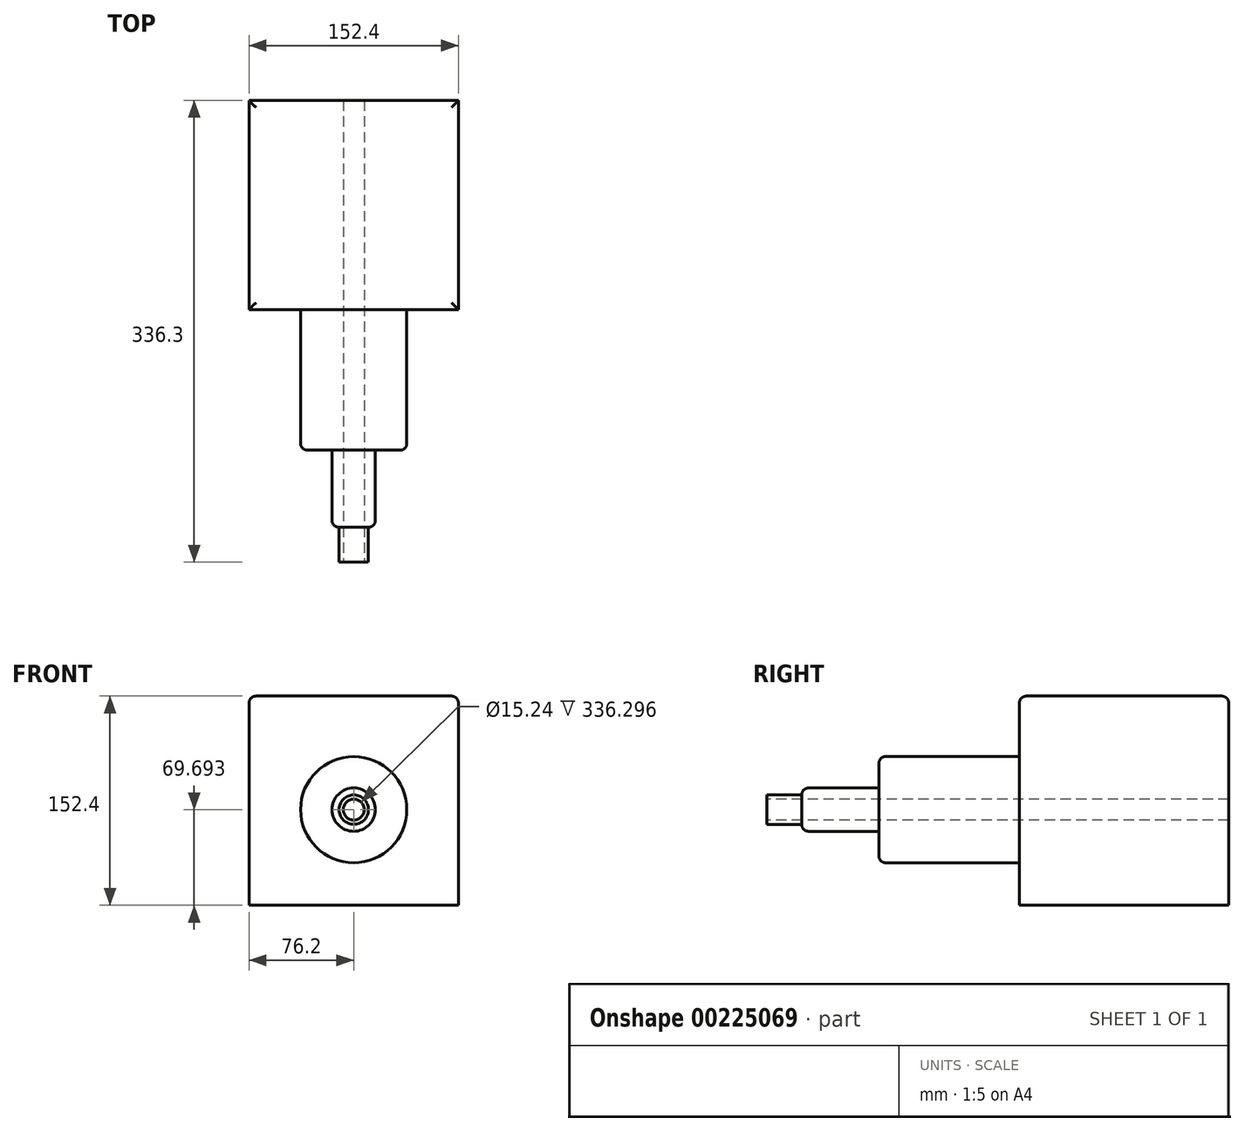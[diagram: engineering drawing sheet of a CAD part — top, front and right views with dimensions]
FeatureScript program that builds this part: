
annotation { "Feature Type Name" : "Feature", "Feature Type Description" : "" }
export const myFeature = defineFeature(function(context is Context, id is Id, definition is map)
    precondition{}
    {
        {
            var Q0;
            Q0=qCreatedBy(makeId("Top.planeOp"),FACE);
            var sketch = newSketch(context, id + "F0", { "sketchPlane" : qUnion([Q0])});
            skLineSegment(sketch, "E0.bottom", {"start": v(76.2, 76.2) * mm, "end": v(-76.2, 76.2) * mm});
            skLineSegment(sketch, "E0.top", {"start": v(76.2, -76.2) * mm, "end": v(-76.2, -76.2) * mm});
            skLineSegment(sketch, "E0.left", {"start": v(76.2, 76.2) * mm, "end": v(76.2, -76.2) * mm});
            skLineSegment(sketch, "E0.right", {"start": v(-76.2, 76.2) * mm, "end": v(-76.2, -76.2) * mm});
            skPoint(sketch, "E0.middle", {"position": v(0, 0) * mm});
            skSolve(sketch);
        }
        {
            var Q0;
            Q0 = qSketchRegion(id + "F0", true);
            extrude(context, id + "F1", {"entities" : qUnion([Q0]), "depth" : 152.4 * mm});
        }
        {
            var Q0;
            Q0=makeQuery(id+"F1.opExtrude","CAP_FACE",FACE,{"disambiguationData":[OSD([sQuery(id+"F0.wireOp",EDGE,"E0.bottom"),sQuery(id+"F0.wireOp",EDGE,"E0.top"),sQuery(id+"F0.wireOp",EDGE,"E0.left"),sQuery(id+"F0.wireOp",EDGE,"E0.right")])],"isStart":false});
            fillet(context, id + "F2", {"entities" : qUnion([Q0]), "radius" : 5.08 * mm, "tangentPropagation" : true, "allowEdgeOverflow" : false});
        }
        {
            var Q0;
            Q0=makeQuery(id+"F1.opExtrude","SWEPT_FACE",FACE,{"disambiguationData":[OSD([sQuery(id+"F0.wireOp",EDGE,"E0.top")])]});
            var sketch = newSketch(context, id + "F3", { "sketchPlane" : qUnion([Q0])});
            skCircle(sketch, "E1", {"center": v(0, 69.7) * mm, "radius": 38.66 * mm});
            skSolve(sketch);
        }
        {
            var Q0;
            Q0 = qSketchRegion(id + "F3", true);
            extrude(context, id + "F4", {"entities" : qUnion([Q0]), "operationType" : NewBodyOperationType.ADD, "depth" : 102.36 * mm});
        }
        {
            var Q0;
            Q0=makeQuery(id+"F4.opExtrude","CAP_FACE",FACE,{"disambiguationData":[OSD([sQuery(id+"F3.wireOp",EDGE,"E1")])],"isStart":false});
            var sketch = newSketch(context, id + "F5", { "sketchPlane" : qUnion([Q0])});
            skCircle(sketch, "E2", {"center": v(0, 69.7) * mm, "radius": 15.78 * mm});
            skSolve(sketch);
        }
        {
            var Q0;
            Q0 = qSketchRegion(id + "F5", true);
            extrude(context, id + "F6", {"entities" : qUnion([Q0]), "operationType" : NewBodyOperationType.ADD, "depth" : 56.13 * mm});
        }
        {
            var Q0;
            Q0=makeQuery(id+"F6.opExtrude","CAP_EDGE",EDGE,{"disambiguationData":[OSD([sQuery(id+"F5.wireOp",EDGE,"E2")])],"isStart":false});
            var Q1;
            Q1=makeQuery(id+"F6.opExtrude","CAP_EDGE",EDGE,{"disambiguationData":[OSD([sQuery(id+"F5.wireOp",EDGE,"E2")])],"isStart":true});
            var Q2;
            Q2=makeQuery(id+"F4.opExtrude","CAP_EDGE",EDGE,{"disambiguationData":[OSD([sQuery(id+"F3.wireOp",EDGE,"E1")])],"isStart":false});
            var Q3;
            Q3=makeQuery(id+"F4.opExtrude","CAP_EDGE",EDGE,{"disambiguationData":[OSD([sQuery(id+"F3.wireOp",EDGE,"E1")])],"isStart":true});
            fillet(context, id + "F7", {"entities" : qUnion([Q0, Q1, Q2, Q3]), "radius" : 5.08 * mm, "tangentPropagation" : true, "allowEdgeOverflow" : false});
        }
        {
            var Q0;
            Q0=makeQuery(id+"F6.opExtrude","CAP_FACE",FACE,{"disambiguationData":[OSD([sQuery(id+"F5.wireOp",EDGE,"E2")])],"isStart":false});
            var sketch = newSketch(context, id + "F8", { "sketchPlane" : qUnion([Q0])});
            skCircle(sketch, "E3", {"center": v(0, 69.7) * mm, "radius": 5.43 * mm});
            skSolve(sketch);
        }
        {
            var Q0;
            Q0=sQuery(id+"F8.wireOp",VERTEX,"E3.center");
            var Q1;
            Q1=makeQuery(id+"F1.opExtrude","SWEPT_BODY",BODY,{"disambiguationData":[OSD([sQuery(id+"F0.wireOp",EDGE,"E0.bottom"),sQuery(id+"F0.wireOp",EDGE,"E0.top"),sQuery(id+"F0.wireOp",EDGE,"E0.left"),sQuery(id+"F0.wireOp",EDGE,"E0.right")])]});
            hole(context, id + "F9", {"style" : HoleStyle.SIMPLE, "endStyle" : HoleEndStyle.THROUGH, "holeDiameter" : 15.24 * mm, "startFromSketch" : true, "locations" : qUnion([Q0]), "scope" : qUnion([Q1]), "isTappedThrough" : true});
        }
        {
            var Q0;
            Q0=makeQuery(id+"F6.opExtrude","CAP_FACE",FACE,{"disambiguationData":[OSD([sQuery(id+"F5.wireOp",EDGE,"E2")])],"isStart":false});
            extrude(context, id + "F10", {"entities" : qUnion([Q0]), "operationType" : NewBodyOperationType.ADD, "depth" : 25.4 * mm});
        }
    });
